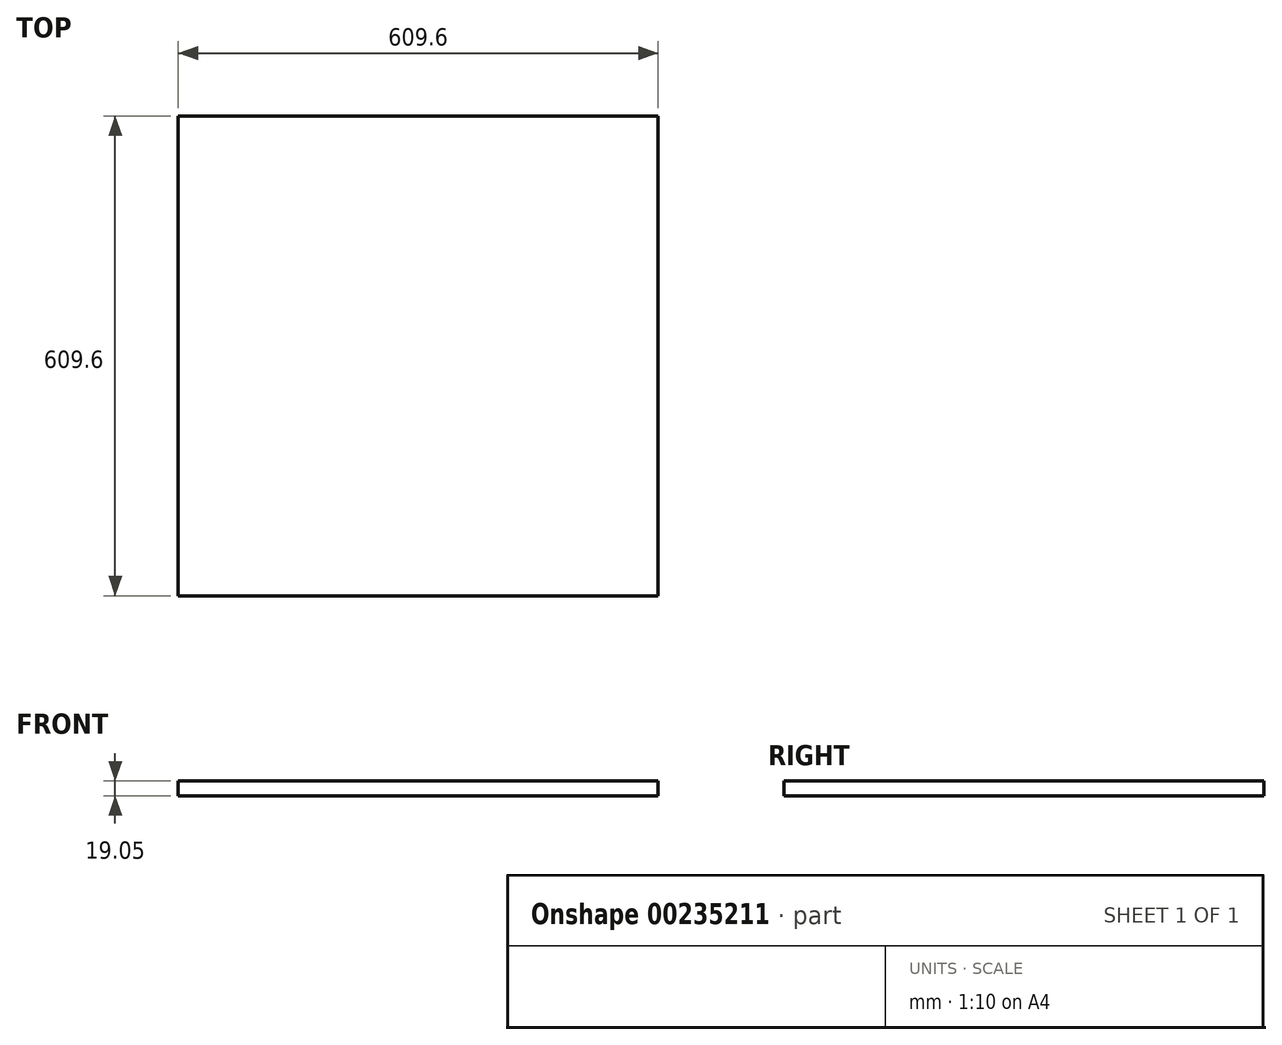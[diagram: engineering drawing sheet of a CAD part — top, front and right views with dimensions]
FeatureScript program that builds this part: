
annotation { "Feature Type Name" : "Feature", "Feature Type Description" : "" }
export const myFeature = defineFeature(function(context is Context, id is Id, definition is map)
    precondition{}
    {
        {
            var Q0;
            Q0=qCreatedBy(makeId("Top.planeOp"),FACE);
            var sketch = newSketch(context, id + "F0", { "sketchPlane" : qUnion([Q0])});
            skLineSegment(sketch, "E0.bottom", {"start": v(304.8, 304.8) * mm, "end": v(-304.8, 304.8) * mm});
            skLineSegment(sketch, "E0.top", {"start": v(304.8, -304.8) * mm, "end": v(-304.8, -304.8) * mm});
            skLineSegment(sketch, "E0.left", {"start": v(304.8, 304.8) * mm, "end": v(304.8, -304.8) * mm});
            skLineSegment(sketch, "E0.right", {"start": v(-304.8, 304.8) * mm, "end": v(-304.8, -304.8) * mm});
            skPoint(sketch, "E0.middle", {"position": v(0, 0) * mm});
            skSolve(sketch);
        }
        {
            var Q0;
            Q0=makeQuery(id+"F0.imprint","IMPRINT",FACE,{"disambiguationData":[TD([[makeQuery(id+"F0.imprint","IMPRINT",EDGE,{"derivedFrom":sQuery(id+"F0.wireOp",EDGE,"E0.bottom")}),1.0]])]});
            extrude(context, id + "F1", {"entities" : qUnion([Q0]), "depth" : 19.05 * mm});
        }
    });
